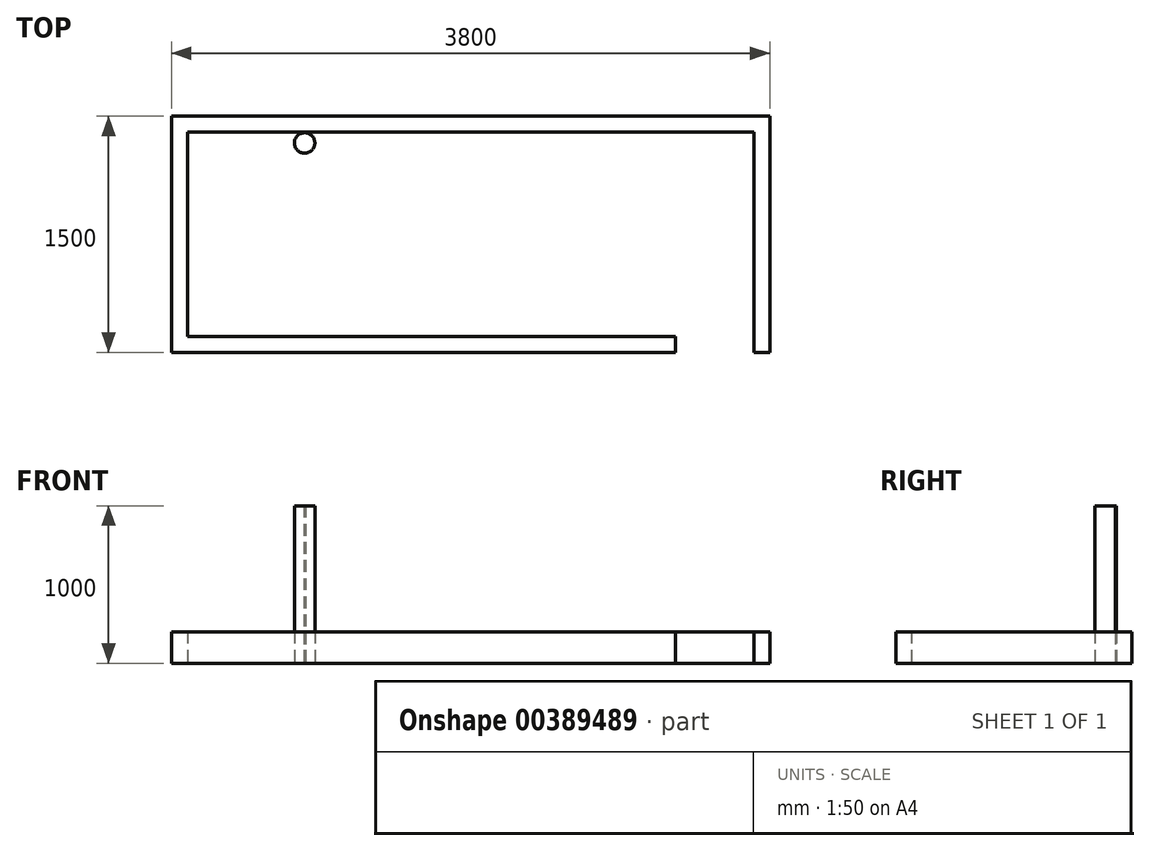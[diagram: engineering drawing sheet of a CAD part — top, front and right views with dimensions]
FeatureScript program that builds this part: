
annotation { "Feature Type Name" : "Feature", "Feature Type Description" : "" }
export const myFeature = defineFeature(function(context is Context, id is Id, definition is map)
    precondition{}
    {
        {
            var Q0;
            Q0=qCreatedBy(makeId("Top.planeOp"),FACE);
            var sketch = newSketch(context, id + "F0", { "sketchPlane" : qUnion([Q0])});
            skLineSegment(sketch, "E0.bottom", {"start": v(-1947.23, 596.42) * mm, "end": v(1652.77, 596.42) * mm});
            skLineSegment(sketch, "E0.top", {"start": v(-1947.23, -703.58) * mm, "end": v(1152.77, -703.58) * mm});
            skLineSegment(sketch, "E0.left", {"start": v(-1947.23, 596.42) * mm, "end": v(-1947.23, -703.58) * mm});
            skLineSegment(sketch, "E0.right", {"start": v(1652.77, 596.42) * mm, "end": v(1652.77, -803.58) * mm});
            skLineSegment(sketch, "E1.0", {"start": v(1752.77, 696.42) * mm, "end": v(1752.77, -803.58) * mm});
            skLineSegment(sketch, "E1.1", {"start": v(-2047.23, 696.42) * mm, "end": v(1752.77, 696.42) * mm});
            skLineSegment(sketch, "E1.2", {"start": v(-2047.23, 696.42) * mm, "end": v(-2047.23, -803.58) * mm});
            skLineSegment(sketch, "E1.3", {"start": v(-2047.23, -803.58) * mm, "end": v(1152.77, -803.58) * mm});
            skLineSegment(sketch, "E2", {"start": v(1152.77, -703.58) * mm, "end": v(1152.77, -803.58) * mm});
            skLineSegment(sketch, "E3", {"start": v(1652.77, -803.58) * mm, "end": v(1752.77, -803.58) * mm});
            skCircle(sketch, "E4", {"center": v(-1202.23, 526.8) * mm, "radius": 65 * mm});
            skPoint(sketch, "E5.middle", {"position": v(-1146.51, 596.42) * mm});
            skLineSegment(sketch, "E6", {"start": v(-1196.2, 591.52) * mm, "end": v(-1196.2, 596.42) * mm});
            skLineSegment(sketch, "E7", {"start": v(-1206.39, 591.66) * mm, "end": v(-1206.39, 596.42) * mm});
            skSolve(sketch);
        }
        {
            var Q0;
            Q0=makeQuery(id+"F0.imprint","IMPRINT",FACE,{"disambiguationData":[TD([[makeQuery(id+"F0.imprint","IMPRINT",EDGE,{"derivedFrom":sQuery(id+"F0.wireOp",EDGE,"E0.bottom")}),1.0]])]});
            extrude(context, id + "F1", {"entities" : qUnion([Q0]), "depth" : 200 * mm});
        }
        {
            var Q0;
            {var subQ0=sQuery(id+"F0.wireOp",EDGE,"E4");var subQ1=makeQuery(id+"F0.imprint","INTERSECT",VERTEX,{"derivedFrom":[subQ0,sQuery(id+"F0.wireOp",EDGE,"E6")]});Q0=makeQuery(id+"F0.imprint","IMPRINT",FACE,{"disambiguationData":[TD([[makeQuery(id+"F0.imprint","IMPRINT",EDGE,{"disambiguationData":[TD([[subQ1,-1.0]])],"derivedFrom":subQ0}),1.0]])]});}
            var Q1;
            {var subQ0=sQuery(id+"F0.wireOp",EDGE,"E6");Q1=makeQuery(id+"F0.imprint","IMPRINT",FACE,{"disambiguationData":[TD([[makeQuery(id+"F0.imprint","IMPRINT",EDGE,{"derivedFrom":subQ0}),1.0]])]});}
            extrude(context, id + "F2", {"entities" : qUnion([Q0, Q1]), "operationType" : NewBodyOperationType.ADD, "depth" : 1000 * mm});
        }
    });
